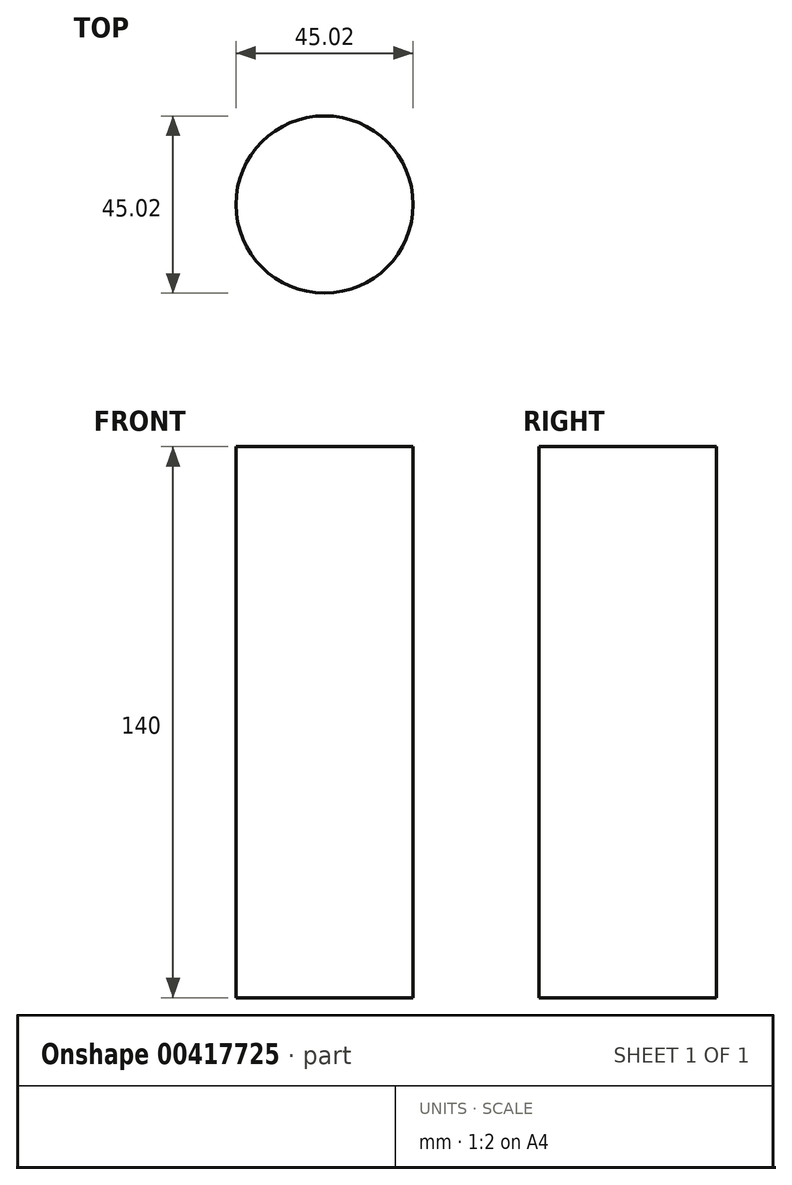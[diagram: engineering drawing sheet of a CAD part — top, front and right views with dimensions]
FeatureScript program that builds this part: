
annotation { "Feature Type Name" : "Feature", "Feature Type Description" : "" }
export const myFeature = defineFeature(function(context is Context, id is Id, definition is map)
    precondition{}
    {
        {
            var Q0;
            Q0=qCreatedBy(makeId("Top.planeOp"),FACE);
            var sketch = newSketch(context, id + "F0", { "sketchPlane" : qUnion([Q0])});
            skCircle(sketch, "E0", {"center": v(0, 0) * mm, "radius": 22.5 * mm});
            skSolve(sketch);
        }
        {
            var Q0;
            Q0=sQuery(id+"F0.wireOp",EDGE,"E0");
            extrude(context, id + "F1", {"bodyType" : ToolBodyType.SURFACE, "surfaceEntities" : qUnion([Q0]), "depth" : 140 * mm});
        }
    });
